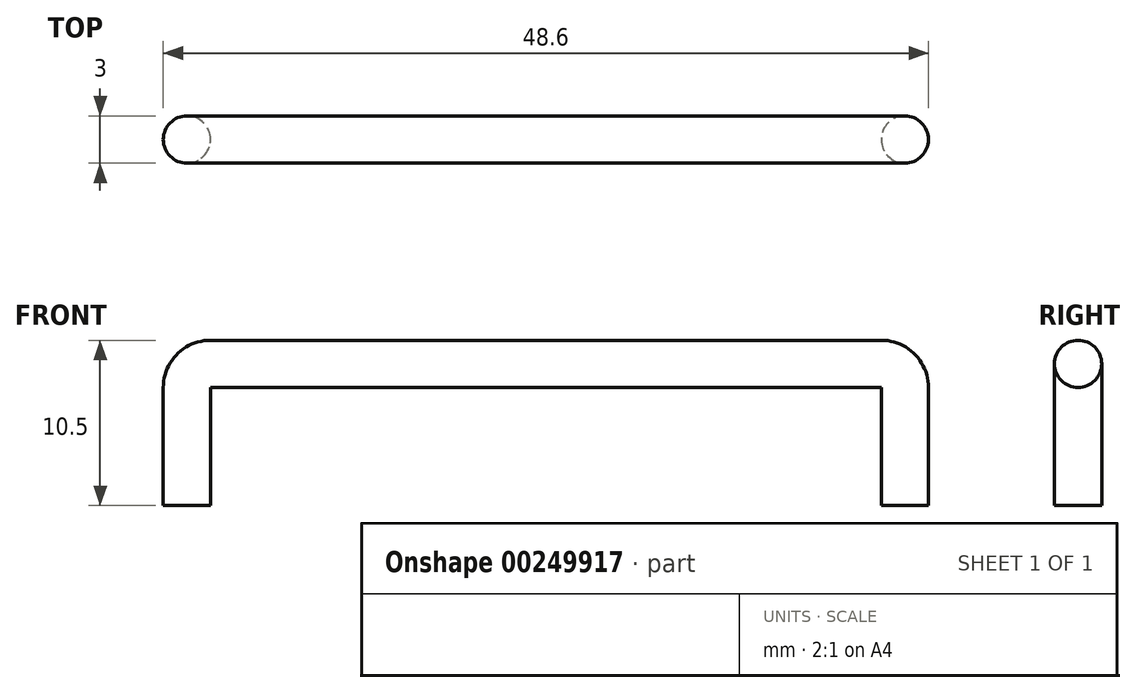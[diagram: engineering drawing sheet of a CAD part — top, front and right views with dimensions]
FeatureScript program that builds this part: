
annotation { "Feature Type Name" : "Feature", "Feature Type Description" : "" }
export const myFeature = defineFeature(function(context is Context, id is Id, definition is map)
    precondition{}
    {
        {
            var Q0;
            Q0=qCreatedBy(makeId("Front.planeOp"),FACE);
            var sketch = newSketch(context, id + "F0", { "sketchPlane" : qUnion([Q0])});
            skLineSegment(sketch, "E0", {"start": v(0, 0) * mm, "end": v(0, 7.5) * mm});
            skLineSegment(sketch, "E1", {"start": v(1.5, 9) * mm, "end": v(44.1, 9) * mm});
            skLineSegment(sketch, "E2", {"start": v(45.6, 7.5) * mm, "end": v(45.6, 0) * mm});
            skArc(sketch, "E3", {"start": v(1.5, 9) * mm, "mid": v(0.44, 8.56) * mm, "end": v(0, 7.5) * mm});
            skArc(sketch, "E4", {"start": v(45.6, 7.5) * mm, "mid": v(45.16, 8.56) * mm, "end": v(44.1, 9) * mm});
            skSolve(sketch);
        }
        {
            var Q0;
            Q0=sQuery(id+"F0.wireOp",VERTEX,"E2.end");
            var Q1;
            Q1=sQuery(id+"F0.wireOp",EDGE,"E2");
            cPlane(context, id + "F1", {"entities" : qUnion([Q0, Q1]), "cplaneType" : CPlaneType.CURVE_POINT, "offset" : 25 * mm, "width" : 150 * mm, "height" : 150 * mm});
        }
        {
            var Q0;
            Q0=qCreatedBy(id+"F1.planeOp",FACE);
            var sketch = newSketch(context, id + "F2", { "sketchPlane" : qUnion([Q0])});
            skCircle(sketch, "E5", {"center": v(84.23, 0) * mm, "radius": 1.5 * mm});
            skCircle(sketch, "E6", {"center": v(45.6, 0) * mm, "radius": 1.5 * mm});
            skSolve(sketch);
        }
        {
            var Q0;
            Q0=makeQuery(id+"F2.imprint","IMPRINT",FACE,{"disambiguationData":[TD([[makeQuery(id+"F2.imprint","IMPRINT",EDGE,{"derivedFrom":sQuery(id+"F2.wireOp",EDGE,"E6")}),1.0]])]});
            var Q1;
            Q1=sQuery(id+"F0.wireOp",EDGE,"E2");
            var Q2;
            Q2=sQuery(id+"F0.wireOp",EDGE,"E1");
            var Q3;
            Q3=sQuery(id+"F0.wireOp",EDGE,"E4");
            var Q4;
            Q4=sQuery(id+"F0.wireOp",EDGE,"E3");
            var Q5;
            Q5=sQuery(id+"F0.wireOp",EDGE,"E0");
            sweep(context, id + "F3", {"profiles" : qUnion([Q0]), "path" : qUnion([Q1, Q2, Q3, Q4, Q5])});
        }
    });
